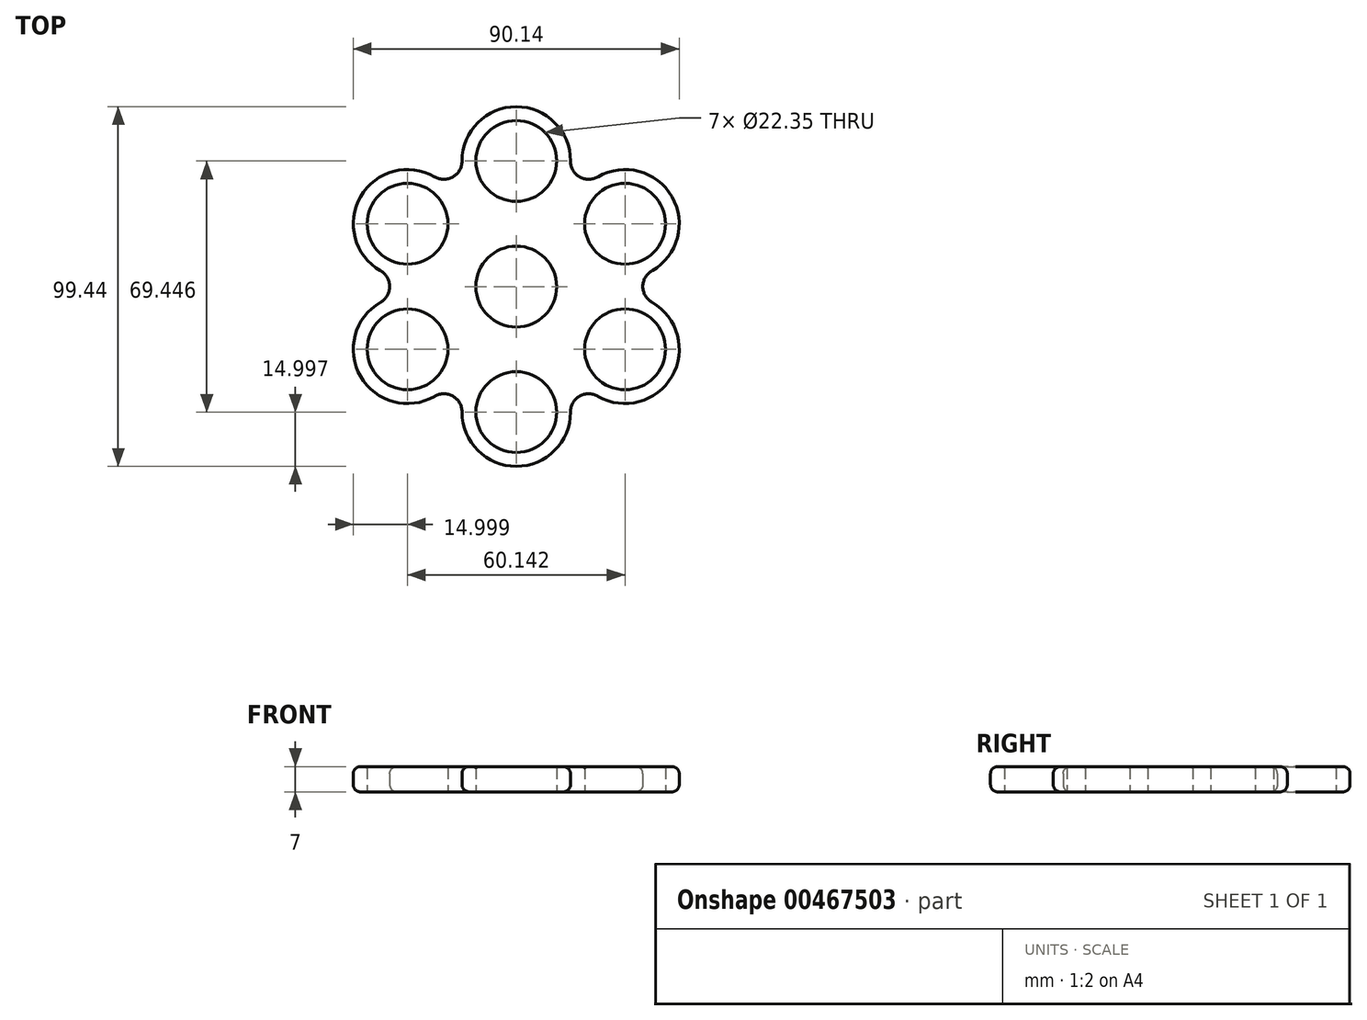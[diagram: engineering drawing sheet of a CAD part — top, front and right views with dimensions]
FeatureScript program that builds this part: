
annotation { "Feature Type Name" : "Feature", "Feature Type Description" : "" }
export const myFeature = defineFeature(function(context is Context, id is Id, definition is map)
    precondition{}
    {
        {
            var Q0;
            Q0=qCreatedBy(makeId("Top.planeOp"),FACE);
            var sketch = newSketch(context, id + "F0", { "sketchPlane" : qUnion([Q0])});
            skCircle(sketch, "E0", {"center": v(0, 34.72) * mm, "radius": 11.18 * mm});
            skLineSegment(sketch, "E1", {"start": v(0, 0) * mm, "end": v(0, 34.72) * mm, "construction": true});
            skCircle(sketch, "E2", {"center": v(0, 34.72) * mm, "radius": 15 * mm});
            skCircle(sketch, "E3", {"center": v(0, 0) * mm, "radius": 11.18 * mm});
            skLineSegment(sketch, "E4", {"start": v(-15, 34.72) * mm, "end": v(-15, 0) * mm});
            skLineSegment(sketch, "E5", {"start": v(15, 34.72) * mm, "end": v(15, 0) * mm});
            skLineSegment(sketch, "E6", {"start": v(-15, 0) * mm, "end": v(15, 0) * mm});
            skLineSegment(sketch, "E7.1.0", {"start": v(-37.57, 4.37) * mm, "end": v(-7.5, -13) * mm});
            skCircle(sketch, "E7.1.1", {"center": v(-30.07, 17.36) * mm, "radius": 15 * mm});
            skCircle(sketch, "E7.1.2", {"center": v(-30.07, 17.36) * mm, "radius": 11.18 * mm});
            skLineSegment(sketch, "E7.1.3", {"start": v(-22.57, 30.35) * mm, "end": v(7.5, 13) * mm});
            skLineSegment(sketch, "E7.2.0", {"start": v(-22.57, -30.35) * mm, "end": v(7.5, -13) * mm});
            skCircle(sketch, "E7.2.1", {"center": v(-30.07, -17.36) * mm, "radius": 15 * mm});
            skCircle(sketch, "E7.2.2", {"center": v(-30.07, -17.36) * mm, "radius": 11.17 * mm});
            skLineSegment(sketch, "E7.2.3", {"start": v(-37.57, -4.37) * mm, "end": v(-7.5, 13) * mm});
            skLineSegment(sketch, "E7.3.0", {"start": v(15, -34.72) * mm, "end": v(15, 0) * mm});
            skCircle(sketch, "E7.3.1", {"center": v(0, -34.72) * mm, "radius": 15 * mm});
            skCircle(sketch, "E7.3.2", {"center": v(0, -34.72) * mm, "radius": 11.18 * mm});
            skLineSegment(sketch, "E7.3.3", {"start": v(-15, -34.72) * mm, "end": v(-15, 0) * mm});
            skLineSegment(sketch, "E8.2.4.0", {"start": v(37.57, -4.37) * mm, "end": v(7.5, 13) * mm});
            skCircle(sketch, "E8.3.4.0", {"center": v(30.07, -17.36) * mm, "radius": 15 * mm});
            skCircle(sketch, "E8.5.4.0", {"center": v(30.07, -17.36) * mm, "radius": 11.18 * mm});
            skLineSegment(sketch, "E8.7.4.0", {"start": v(22.57, -30.35) * mm, "end": v(-7.5, -13) * mm});
            skLineSegment(sketch, "E8.2.5.0", {"start": v(22.57, 30.35) * mm, "end": v(-7.5, 13) * mm});
            skCircle(sketch, "E8.3.5.0", {"center": v(30.07, 17.36) * mm, "radius": 15 * mm});
            skCircle(sketch, "E8.5.5.0", {"center": v(30.07, 17.36) * mm, "radius": 11.18 * mm});
            skLineSegment(sketch, "E8.7.5.0", {"start": v(37.57, 4.37) * mm, "end": v(7.5, -13) * mm});
            skSolve(sketch);
        }
        {
            var Q0;
            Q0=makeQuery(id+"F0.imprint","IMPRINT",FACE,{"disambiguationData":[TD([[makeQuery(id+"F0.imprint","IMPRINT",EDGE,{"derivedFrom":sQuery(id+"F0.wireOp",EDGE,"36e7d391-d642-43d3-ac27-a5ee1db5424b.1.0")}),-1.0]])]});
            var Q1;
            {var subQ7=sQuery(id+"F0.wireOp",EDGE,"E6");var subQ10=sQuery(id+"F0.wireOp",EDGE,"E3");var subQ14=makeQuery(id+"F0.imprint","INTERSECT",VERTEX,{"disambiguationData":[OD(0.0)],"derivedFrom":[subQ10,subQ7]});Q1=makeQuery(id+"F0.imprint","IMPRINT",FACE,{"disambiguationData":[TD([[makeQuery(id+"F0.imprint","IMPRINT",EDGE,{"disambiguationData":[TD([[subQ14,-1.0]])],"derivedFrom":subQ10}),-1.0]])]});}
            var Q2;
            Q2=makeQuery(id+"F0.imprint","IMPRINT",FACE,{"disambiguationData":[TD([[makeQuery(id+"F0.imprint","IMPRINT",EDGE,{"derivedFrom":sQuery(id+"F0.wireOp",EDGE,"36e7d391-d642-43d3-ac27-a5ee1db5424b.2.0")}),-1.0]])]});
            var Q3;
            {var subQ1=sQuery(id+"F0.wireOp",EDGE,"E4");var subQ4=sQuery(id+"F0.wireOp",EDGE,"E2");var subQ5=makeQuery(id+"F0.imprint","INTERSECT",VERTEX,{"derivedFrom":[subQ4,subQ1]});Q3=makeQuery(id+"F0.imprint","IMPRINT",FACE,{"disambiguationData":[TD([[makeQuery(id+"F0.imprint","IMPRINT",EDGE,{"disambiguationData":[TD([[subQ5,-1.0]])],"derivedFrom":subQ4}),-1.0]])]});}
            var Q4;
            Q4=makeQuery(id+"F0.imprint","IMPRINT",FACE,{"disambiguationData":[TD([[makeQuery(id+"F0.imprint","IMPRINT",EDGE,{"derivedFrom":sQuery(id+"F0.wireOp",EDGE,"E0")}),-1.0]])]});
            var Q5;
            Q5=makeQuery(id+"F0.imprint","IMPRINT",FACE,{"disambiguationData":[TD([[makeQuery(id+"F0.imprint","IMPRINT",EDGE,{"derivedFrom":sQuery(id+"F0.wireOp",EDGE,"E7.1.2")}),-1.0]])]});
            var Q6;
            {var subQ10=sQuery(id+"F0.wireOp",EDGE,"E7.1.3");var subQ15=sQuery(id+"F0.wireOp",EDGE,"E2");var subQ16=makeQuery(id+"F0.imprint","INTERSECT",VERTEX,{"derivedFrom":[subQ15,subQ10]});Q6=makeQuery(id+"F0.imprint","IMPRINT",FACE,{"disambiguationData":[TD([[makeQuery(id+"F0.imprint","IMPRINT",EDGE,{"disambiguationData":[TD([[subQ16,-1.0]])],"derivedFrom":subQ15}),-1.0]])]});}
            var Q7;
            {var subQ0=sQuery(id+"F0.wireOp",EDGE,"E7.1.3");var subQ1=sQuery(id+"F0.wireOp",EDGE,"E2");var subQ2=makeQuery(id+"F0.imprint","INTERSECT",VERTEX,{"derivedFrom":[subQ1,subQ0]});Q7=makeQuery(id+"F0.imprint","IMPRINT",FACE,{"disambiguationData":[TD([[makeQuery(id+"F0.imprint","IMPRINT",EDGE,{"disambiguationData":[TD([[subQ2,-1.0]])],"derivedFrom":subQ1}),1.0]])]});}
            var Q8;
            {var subQ1=sQuery(id+"F0.wireOp",EDGE,"E4");var subQ3=sQuery(id+"F0.wireOp",EDGE,"E7.1.1");var subQ4=makeQuery(id+"F0.imprint","INTERSECT",VERTEX,{"derivedFrom":[subQ1,subQ3]});Q8=makeQuery(id+"F0.imprint","IMPRINT",FACE,{"disambiguationData":[TD([[makeQuery(id+"F0.imprint","IMPRINT",EDGE,{"disambiguationData":[TD([[subQ4,1.0]])],"derivedFrom":subQ3}),1.0]])]});}
            var Q9;
            {var subQ1=sQuery(id+"F0.wireOp",EDGE,"E6");var subQ3=sQuery(id+"F0.wireOp",EDGE,"E7.1.1");var subQ4=makeQuery(id+"F0.imprint","INTERSECT",VERTEX,{"derivedFrom":[subQ1,subQ3]});Q9=makeQuery(id+"F0.imprint","IMPRINT",FACE,{"disambiguationData":[TD([[makeQuery(id+"F0.imprint","IMPRINT",EDGE,{"disambiguationData":[TD([[subQ4,1.0]])],"derivedFrom":subQ3}),1.0]])]});}
            var Q10;
            Q10=makeQuery(id+"F0.imprint","IMPRINT",FACE,{"disambiguationData":[TD([[makeQuery(id+"F0.imprint","IMPRINT",EDGE,{"derivedFrom":sQuery(id+"F0.wireOp",EDGE,"E7.3.2")}),-1.0]])]});
            var Q11;
            {var subQ0=sQuery(id+"F0.wireOp",EDGE,"E7.3.3");var subQ1=sQuery(id+"F0.wireOp",EDGE,"E7.2.0");var subQ2=makeQuery(id+"F0.imprint","INTERSECT",VERTEX,{"derivedFrom":[subQ1,subQ0]});Q11=makeQuery(id+"F0.imprint","IMPRINT",FACE,{"disambiguationData":[TD([[makeQuery(id+"F0.imprint","IMPRINT",EDGE,{"disambiguationData":[TD([[subQ2,-1.0]])],"derivedFrom":subQ1}),-1.0]])]});}
            var Q12;
            {var subQ1=sQuery(id+"F0.wireOp",EDGE,"E6");var subQ3=sQuery(id+"F0.wireOp",EDGE,"E7.3.1");var subQ4=makeQuery(id+"F0.imprint","INTERSECT",VERTEX,{"derivedFrom":[subQ1,subQ3]});Q12=makeQuery(id+"F0.imprint","IMPRINT",FACE,{"disambiguationData":[TD([[makeQuery(id+"F0.imprint","IMPRINT",EDGE,{"disambiguationData":[TD([[subQ4,-1.0]])],"derivedFrom":subQ3}),1.0]])]});}
            var Q13;
            {var subQ1=sQuery(id+"F0.wireOp",EDGE,"E5");var subQ3=sQuery(id+"F0.wireOp",EDGE,"E7.3.1");var subQ4=makeQuery(id+"F0.imprint","INTERSECT",VERTEX,{"derivedFrom":[subQ1,subQ3]});Q13=makeQuery(id+"F0.imprint","IMPRINT",FACE,{"disambiguationData":[TD([[makeQuery(id+"F0.imprint","IMPRINT",EDGE,{"disambiguationData":[TD([[subQ4,-1.0]])],"derivedFrom":subQ3}),1.0]])]});}
            var Q14;
            {var subQ0=sQuery(id+"F0.wireOp",EDGE,"E7.3.0");var subQ1=sQuery(id+"F0.wireOp",EDGE,"E5");var subQ2=makeQuery(id+"F0.imprint","INTERSECT",VERTEX,{"derivedFrom":[subQ1,subQ0]});Q14=makeQuery(id+"F0.imprint","IMPRINT",FACE,{"disambiguationData":[TD([[makeQuery(id+"F0.imprint","IMPRINT",EDGE,{"disambiguationData":[TD([[subQ2,-1.0]])],"derivedFrom":subQ1}),1.0]])]});}
            var Q15;
            {var subQ0=sQuery(id+"F0.wireOp",EDGE,"E5");var subQ1=sQuery(id+"F0.wireOp",EDGE,"E2");var subQ2=makeQuery(id+"F0.imprint","INTERSECT",VERTEX,{"derivedFrom":[subQ1,subQ0]});Q15=makeQuery(id+"F0.imprint","IMPRINT",FACE,{"disambiguationData":[TD([[makeQuery(id+"F0.imprint","IMPRINT",EDGE,{"disambiguationData":[TD([[subQ2,1.0]])],"derivedFrom":subQ1}),-1.0]])]});}
            var Q16;
            Q16=makeQuery(id+"F0.imprint","IMPRINT",FACE,{"disambiguationData":[TD([[makeQuery(id+"F0.imprint","IMPRINT",EDGE,{"derivedFrom":sQuery(id+"F0.wireOp",EDGE,"E7.2.2")}),-1.0]])]});
            var Q17;
            {var subQ0=sQuery(id+"F0.wireOp",EDGE,"E7.2.1");var subQ1=sQuery(id+"F0.wireOp",EDGE,"E7.2.0");var subQ2=makeQuery(id+"F0.imprint","INTERSECT",VERTEX,{"derivedFrom":[subQ1,subQ0]});Q17=makeQuery(id+"F0.imprint","IMPRINT",FACE,{"disambiguationData":[TD([[makeQuery(id+"F0.imprint","IMPRINT",EDGE,{"disambiguationData":[TD([[subQ2,-1.0]])],"derivedFrom":subQ1}),1.0]])]});}
            var Q18;
            {var subQ0=sQuery(id+"F0.wireOp",EDGE,"E7.3.3");var subQ1=sQuery(id+"F0.wireOp",EDGE,"E7.1.0");var subQ2=makeQuery(id+"F0.imprint","INTERSECT",VERTEX,{"derivedFrom":[subQ1,subQ0]});Q18=makeQuery(id+"F0.imprint","IMPRINT",FACE,{"disambiguationData":[TD([[makeQuery(id+"F0.imprint","IMPRINT",EDGE,{"disambiguationData":[TD([[subQ2,1.0]])],"derivedFrom":subQ1}),1.0]])]});}
            var Q19;
            {var subQ0=sQuery(id+"F0.wireOp",EDGE,"E7.2.3");var subQ1=sQuery(id+"F0.wireOp",EDGE,"E7.1.0");var subQ2=makeQuery(id+"F0.imprint","INTERSECT",VERTEX,{"derivedFrom":[subQ1,subQ0]});Q19=makeQuery(id+"F0.imprint","IMPRINT",FACE,{"disambiguationData":[TD([[makeQuery(id+"F0.imprint","IMPRINT",EDGE,{"disambiguationData":[TD([[subQ2,-1.0]])],"derivedFrom":subQ1}),-1.0]])]});}
            var Q20;
            {var subQ0=sQuery(id+"F0.wireOp",EDGE,"E7.1.1");var subQ1=sQuery(id+"F0.wireOp",EDGE,"E7.1.0");var subQ2=makeQuery(id+"F0.imprint","INTERSECT",VERTEX,{"derivedFrom":[subQ1,subQ0]});Q20=makeQuery(id+"F0.imprint","IMPRINT",FACE,{"disambiguationData":[TD([[makeQuery(id+"F0.imprint","IMPRINT",EDGE,{"disambiguationData":[TD([[subQ2,-1.0]])],"derivedFrom":subQ1}),1.0]])]});}
            var Q21;
            {var subQ0=sQuery(id+"F0.wireOp",EDGE,"E7.1.3");var subQ1=sQuery(id+"F0.wireOp",EDGE,"E4");var subQ2=makeQuery(id+"F0.imprint","INTERSECT",VERTEX,{"derivedFrom":[subQ1,subQ0]});Q21=makeQuery(id+"F0.imprint","IMPRINT",FACE,{"disambiguationData":[TD([[makeQuery(id+"F0.imprint","IMPRINT",EDGE,{"disambiguationData":[TD([[subQ2,-1.0]])],"derivedFrom":subQ1}),-1.0]])]});}
            var Q22;
            {var subQ0=sQuery(id+"F0.wireOp",EDGE,"E7.1.3");var subQ1=sQuery(id+"F0.wireOp",EDGE,"E4");var subQ2=makeQuery(id+"F0.imprint","INTERSECT",VERTEX,{"derivedFrom":[subQ1,subQ0]});Q22=makeQuery(id+"F0.imprint","IMPRINT",FACE,{"disambiguationData":[TD([[makeQuery(id+"F0.imprint","IMPRINT",EDGE,{"disambiguationData":[TD([[subQ2,-1.0]])],"derivedFrom":subQ1}),1.0]])]});}
            var Q23;
            {var subQ0=sQuery(id+"F0.wireOp",EDGE,"E6");var subQ3=sQuery(id+"F0.wireOp",EDGE,"E3");var subQ4=makeQuery(id+"F0.imprint","INTERSECT",VERTEX,{"disambiguationData":[OD(0.0)],"derivedFrom":[subQ3,subQ0]});Q23=makeQuery(id+"F0.imprint","IMPRINT",FACE,{"disambiguationData":[TD([[makeQuery(id+"F0.imprint","IMPRINT",EDGE,{"disambiguationData":[TD([[subQ4,1.0]])],"derivedFrom":subQ3}),-1.0]])]});}
            var Q24;
            {var subQ0=sQuery(id+"F0.wireOp",EDGE,"E8.2.5.0");var subQ1=sQuery(id+"F0.wireOp",EDGE,"E5");var subQ2=makeQuery(id+"F0.imprint","INTERSECT",VERTEX,{"derivedFrom":[subQ1,subQ0]});Q24=makeQuery(id+"F0.imprint","IMPRINT",FACE,{"disambiguationData":[TD([[makeQuery(id+"F0.imprint","IMPRINT",EDGE,{"disambiguationData":[TD([[subQ2,-1.0]])],"derivedFrom":subQ1}),-1.0]])]});}
            var Q25;
            {var subQ1=sQuery(id+"F0.wireOp",EDGE,"E8.2.5.0");var subQ3=sQuery(id+"F0.wireOp",EDGE,"E5");var subQ4=makeQuery(id+"F0.imprint","INTERSECT",VERTEX,{"derivedFrom":[subQ3,subQ1]});Q25=makeQuery(id+"F0.imprint","IMPRINT",FACE,{"disambiguationData":[TD([[makeQuery(id+"F0.imprint","IMPRINT",EDGE,{"disambiguationData":[TD([[subQ4,-1.0]])],"derivedFrom":subQ3}),1.0]])]});}
            var Q26;
            Q26=makeQuery(id+"F0.imprint","IMPRINT",FACE,{"disambiguationData":[TD([[makeQuery(id+"F0.imprint","IMPRINT",EDGE,{"derivedFrom":sQuery(id+"F0.wireOp",EDGE,"E8.5.5.0")}),-1.0]])]});
            var Q27;
            {var subQ3=sQuery(id+"F0.wireOp",EDGE,"E8.2.4.0");var subQ5=sQuery(id+"F0.wireOp",EDGE,"E8.7.5.0");var subQ7=makeQuery(id+"F0.imprint","INTERSECT",VERTEX,{"derivedFrom":[subQ3,subQ5]});Q27=makeQuery(id+"F0.imprint","IMPRINT",FACE,{"disambiguationData":[TD([[makeQuery(id+"F0.imprint","IMPRINT",EDGE,{"disambiguationData":[TD([[subQ7,-1.0]])],"derivedFrom":subQ3}),1.0]])]});}
            var Q28;
            Q28=makeQuery(id+"F0.imprint","IMPRINT",FACE,{"disambiguationData":[TD([[makeQuery(id+"F0.imprint","IMPRINT",EDGE,{"derivedFrom":sQuery(id+"F0.wireOp",EDGE,"E8.5.4.0")}),-1.0]])]});
            var Q29;
            {var subQ0=sQuery(id+"F0.wireOp",EDGE,"E8.7.5.0");var subQ1=sQuery(id+"F0.wireOp",EDGE,"E7.2.0");var subQ2=makeQuery(id+"F0.imprint","INTERSECT",VERTEX,{"derivedFrom":[subQ1,subQ0]});Q29=makeQuery(id+"F0.imprint","IMPRINT",FACE,{"disambiguationData":[TD([[makeQuery(id+"F0.imprint","IMPRINT",EDGE,{"disambiguationData":[TD([[subQ2,1.0]])],"derivedFrom":subQ1}),-1.0]])]});}
            var Q30;
            {var subQ0=sQuery(id+"F0.wireOp",EDGE,"E8.7.4.0");var subQ1=sQuery(id+"F0.wireOp",EDGE,"E7.1.0");var subQ2=makeQuery(id+"F0.imprint","INTERSECT",VERTEX,{"derivedFrom":[subQ1,subQ0]});Q30=makeQuery(id+"F0.imprint","IMPRINT",FACE,{"disambiguationData":[TD([[makeQuery(id+"F0.imprint","IMPRINT",EDGE,{"disambiguationData":[TD([[subQ2,1.0]])],"derivedFrom":subQ1}),-1.0]])]});}
            var Q31;
            {var subQ0=sQuery(id+"F0.wireOp",EDGE,"E8.7.4.0");var subQ3=sQuery(id+"F0.wireOp",EDGE,"E7.3.0");var subQ4=makeQuery(id+"F0.imprint","INTERSECT",VERTEX,{"derivedFrom":[subQ3,subQ0]});Q31=makeQuery(id+"F0.imprint","IMPRINT",FACE,{"disambiguationData":[TD([[makeQuery(id+"F0.imprint","IMPRINT",EDGE,{"disambiguationData":[TD([[subQ4,-1.0]])],"derivedFrom":subQ3}),-1.0]])]});}
            extrude(context, id + "F1", {"entities" : qUnion([Q0, Q1, Q2, Q3, Q4, Q5, Q6, Q7, Q8, Q9, Q10, Q11, Q12, Q13, Q14, Q15, Q16, Q17, Q18, Q19, Q20, Q21, Q22, Q23, Q24, Q25, Q26, Q27, Q28, Q29, Q30, Q31]), "depth" : 7 * mm, "offsetDistance" : 25 * mm});
        }
        {
            var Q0;
            Q0=makeQuery(id+"F1.opExtrude","SWEPT_EDGE",EDGE,{"disambiguationData":[OSD([sQuery(id+"F0.wireOp",EDGE,"E4"),sQuery(id+"F0.wireOp",EDGE,"36e7d391-d642-43d3-ac27-a5ee1db5424b.1.2")])]});
            var Q1;
            Q1=makeQuery(id+"F1.opExtrude","SWEPT_EDGE",EDGE,{"disambiguationData":[OSD([sQuery(id+"F0.wireOp",EDGE,"E5"),sQuery(id+"F0.wireOp",EDGE,"36e7d391-d642-43d3-ac27-a5ee1db5424b.2.3")])]});
            var Q2;
            Q2=makeQuery(id+"F1.opExtrude","SWEPT_EDGE",EDGE,{"disambiguationData":[OSD([sQuery(id+"F0.wireOp",EDGE,"36e7d391-d642-43d3-ac27-a5ee1db5424b.1.3"),sQuery(id+"F0.wireOp",EDGE,"36e7d391-d642-43d3-ac27-a5ee1db5424b.2.2")])]});
            var Q3;
            Q3=makeQuery(id+"F1.opExtrude","SWEPT_EDGE",EDGE,{"disambiguationData":[OSD([sQuery(id+"F0.wireOp",EDGE,"E7.2.0"),sQuery(id+"F0.wireOp",EDGE,"E7.3.3")])]});
            var Q4;
            Q4=makeQuery(id+"F1.opExtrude","SWEPT_EDGE",EDGE,{"disambiguationData":[OSD([sQuery(id+"F0.wireOp",EDGE,"E7.1.0"),sQuery(id+"F0.wireOp",EDGE,"E7.2.3")])]});
            var Q5;
            Q5=makeQuery(id+"F1.opExtrude","SWEPT_EDGE",EDGE,{"disambiguationData":[OSD([sQuery(id+"F0.wireOp",EDGE,"E8.2.4.0"),sQuery(id+"F0.wireOp",EDGE,"E8.7.5.0")])]});
            var Q6;
            Q6=makeQuery(id+"F1.opExtrude","SWEPT_EDGE",EDGE,{"disambiguationData":[OSD([sQuery(id+"F0.wireOp",EDGE,"E7.3.0"),sQuery(id+"F0.wireOp",EDGE,"E8.7.4.0")])]});
            fillet(context, id + "F2", {"entities" : qUnion([Q0, Q1, Q2, Q3, Q4, Q5, Q6]), "radius" : 5 * mm, "tangentPropagation" : true, "allowEdgeOverflow" : false});
        }
        {
            var Q0;
            Q0=makeQuery(id+"F1.opExtrude","CAP_EDGE",EDGE,{"disambiguationData":[OSD([sQuery(id+"F0.wireOp",EDGE,"E0")])],"isStart":false});
            var Q1;
            Q1=makeQuery(id+"F1.opExtrude","CAP_EDGE",EDGE,{"disambiguationData":[OSD([sQuery(id+"F0.wireOp",EDGE,"E3")])],"isStart":false});
            var Q2;
            Q2=makeQuery(id+"F1.opExtrude","CAP_EDGE",EDGE,{"disambiguationData":[OSD([sQuery(id+"F0.wireOp",EDGE,"36e7d391-d642-43d3-ac27-a5ee1db5424b.1.0")])],"isStart":false});
            var Q3;
            Q3=makeQuery(id+"F1.opExtrude","CAP_EDGE",EDGE,{"disambiguationData":[OSD([sQuery(id+"F0.wireOp",EDGE,"36e7d391-d642-43d3-ac27-a5ee1db5424b.2.0")])],"isStart":false});
            var Q4;
            Q4=makeQuery(id+"F1.opExtrude","CAP_EDGE",EDGE,{"disambiguationData":[OSD([sQuery(id+"F0.wireOp",EDGE,"36e7d391-d642-43d3-ac27-a5ee1db5424b.1.0")])],"isStart":true});
            var Q5;
            Q5=makeQuery(id+"F1.opExtrude","CAP_EDGE",EDGE,{"disambiguationData":[OSD([sQuery(id+"F0.wireOp",EDGE,"E0")])],"isStart":true});
            var Q6;
            Q6=makeQuery(id+"F1.opExtrude","CAP_EDGE",EDGE,{"disambiguationData":[OSD([sQuery(id+"F0.wireOp",EDGE,"36e7d391-d642-43d3-ac27-a5ee1db5424b.2.0")])],"isStart":true});
            var Q7;
            Q7=makeQuery(id+"F1.opExtrude","CAP_EDGE",EDGE,{"disambiguationData":[OSD([sQuery(id+"F0.wireOp",EDGE,"E3")])],"isStart":true});
            var Q8;
            Q8=makeQuery(id+"F1.opExtrude","CAP_EDGE",EDGE,{"disambiguationData":[OSD([sQuery(id+"F0.wireOp",EDGE,"E7.2.2")])],"isStart":false});
            var Q9;
            Q9=makeQuery(id+"F1.opExtrude","CAP_EDGE",EDGE,{"disambiguationData":[OSD([sQuery(id+"F0.wireOp",EDGE,"E7.1.2")])],"isStart":true});
            var Q10;
            Q10=makeQuery(id+"F1.opExtrude","CAP_EDGE",EDGE,{"disambiguationData":[OSD([sQuery(id+"F0.wireOp",EDGE,"E7.3.2")])],"isStart":true});
            var Q11;
            Q11=makeQuery(id+"F1.opExtrude","CAP_EDGE",EDGE,{"disambiguationData":[OSD([sQuery(id+"F0.wireOp",EDGE,"E7.2.2")])],"isStart":true});
            var Q12;
            Q12=makeQuery(id+"F1.opExtrude","CAP_EDGE",EDGE,{"disambiguationData":[OSD([sQuery(id+"F0.wireOp",EDGE,"E7.3.2")])],"isStart":false});
            var Q13;
            Q13=makeQuery(id+"F1.opExtrude","CAP_EDGE",EDGE,{"disambiguationData":[OSD([sQuery(id+"F0.wireOp",EDGE,"E7.1.2")])],"isStart":false});
            var Q14;
            Q14=makeQuery(id+"F1.opExtrude","CAP_EDGE",EDGE,{"disambiguationData":[OSD([sQuery(id+"F0.wireOp",EDGE,"E8.5.5.0")])],"isStart":false});
            var Q15;
            Q15=makeQuery(id+"F1.opExtrude","CAP_EDGE",EDGE,{"disambiguationData":[OSD([sQuery(id+"F0.wireOp",EDGE,"E8.5.4.0")])],"isStart":false});
            var Q16;
            Q16=makeQuery(id+"F1.opExtrude","CAP_EDGE",EDGE,{"disambiguationData":[OSD([sQuery(id+"F0.wireOp",EDGE,"E8.5.5.0")])],"isStart":true});
            var Q17;
            Q17=makeQuery(id+"F1.opExtrude","CAP_EDGE",EDGE,{"disambiguationData":[OSD([sQuery(id+"F0.wireOp",EDGE,"E8.5.4.0")])],"isStart":true});
            fillet(context, id + "F3", {"entities" : qUnion([Q0, Q1, Q2, Q3, Q4, Q5, Q6, Q7, Q8, Q9, Q10, Q11, Q12, Q13, Q14, Q15, Q16, Q17]), "radius" : .5 * mm, "tangentPropagation" : true, "allowEdgeOverflow" : false});
        }
        {
            var Q0;
            Q0=makeQuery(id+"F1.opExtrude","SWEPT_FACE",FACE,{"disambiguationData":[OSD([sQuery(id+"F0.wireOp",EDGE,"36e7d391-d642-43d3-ac27-a5ee1db5424b.1.3")])]});
            var Q1;
            Q1=makeQuery(id+"F2.opFillet","BLEND_FACE",FACE,{"disambiguationData":[OSD([sQuery(id+"F0.wireOp",EDGE,"36e7d391-d642-43d3-ac27-a5ee1db5424b.1.3"),sQuery(id+"F0.wireOp",EDGE,"36e7d391-d642-43d3-ac27-a5ee1db5424b.2.2")])]});
            var Q2;
            Q2=makeQuery(id+"F1.opExtrude","SWEPT_FACE",FACE,{"disambiguationData":[OSD([sQuery(id+"F0.wireOp",EDGE,"36e7d391-d642-43d3-ac27-a5ee1db5424b.2.2")])]});
            var Q3;
            Q3=makeQuery(id+"F1.opExtrude","SWEPT_FACE",FACE,{"disambiguationData":[OSD([sQuery(id+"F0.wireOp",EDGE,"36e7d391-d642-43d3-ac27-a5ee1db5424b.2.1")])]});
            var Q4;
            Q4=makeQuery(id+"F1.opExtrude","SWEPT_FACE",FACE,{"disambiguationData":[OSD([sQuery(id+"F0.wireOp",EDGE,"36e7d391-d642-43d3-ac27-a5ee1db5424b.1.1")])]});
            var Q5;
            Q5=makeQuery(id+"F1.opExtrude","SWEPT_FACE",FACE,{"disambiguationData":[OSD([sQuery(id+"F0.wireOp",EDGE,"36e7d391-d642-43d3-ac27-a5ee1db5424b.1.2")])]});
            var Q6;
            Q6=makeQuery(id+"F2.opFillet","BLEND_FACE",FACE,{"disambiguationData":[OSD([sQuery(id+"F0.wireOp",EDGE,"E4"),sQuery(id+"F0.wireOp",EDGE,"36e7d391-d642-43d3-ac27-a5ee1db5424b.1.2")])]});
            var Q7;
            Q7=makeQuery(id+"F1.opExtrude","SWEPT_FACE",FACE,{"disambiguationData":[OSD([sQuery(id+"F0.wireOp",EDGE,"E4")])]});
            var Q8;
            Q8=makeQuery(id+"F1.opExtrude","SWEPT_FACE",FACE,{"disambiguationData":[OSD([sQuery(id+"F0.wireOp",EDGE,"E2")])]});
            var Q9;
            Q9=makeQuery(id+"F1.opExtrude","SWEPT_FACE",FACE,{"disambiguationData":[OSD([sQuery(id+"F0.wireOp",EDGE,"E5")])]});
            var Q10;
            Q10=makeQuery(id+"F2.opFillet","BLEND_FACE",FACE,{"disambiguationData":[OSD([sQuery(id+"F0.wireOp",EDGE,"E5"),sQuery(id+"F0.wireOp",EDGE,"36e7d391-d642-43d3-ac27-a5ee1db5424b.2.3")])]});
            var Q11;
            Q11=makeQuery(id+"F1.opExtrude","SWEPT_FACE",FACE,{"disambiguationData":[OSD([sQuery(id+"F0.wireOp",EDGE,"36e7d391-d642-43d3-ac27-a5ee1db5424b.2.3")])]});
            var Q12;
            Q12=makeQuery(id+"F1.opExtrude","CAP_EDGE",EDGE,{"disambiguationData":[OSD([sQuery(id+"F0.wireOp",EDGE,"E7.2.1")])],"isStart":false});
            var Q13;
            Q13=makeQuery(id+"F1.opExtrude","CAP_EDGE",EDGE,{"disambiguationData":[OSD([sQuery(id+"F0.wireOp",EDGE,"E7.2.1")])],"isStart":true});
            fillet(context, id + "F4", {"entities" : qUnion([Q0, Q1, Q2, Q3, Q4, Q5, Q6, Q7, Q8, Q9, Q10, Q11, Q12, Q13]), "radius" : 2 * mm, "tangentPropagation" : true, "allowEdgeOverflow" : false});
        }
    });
